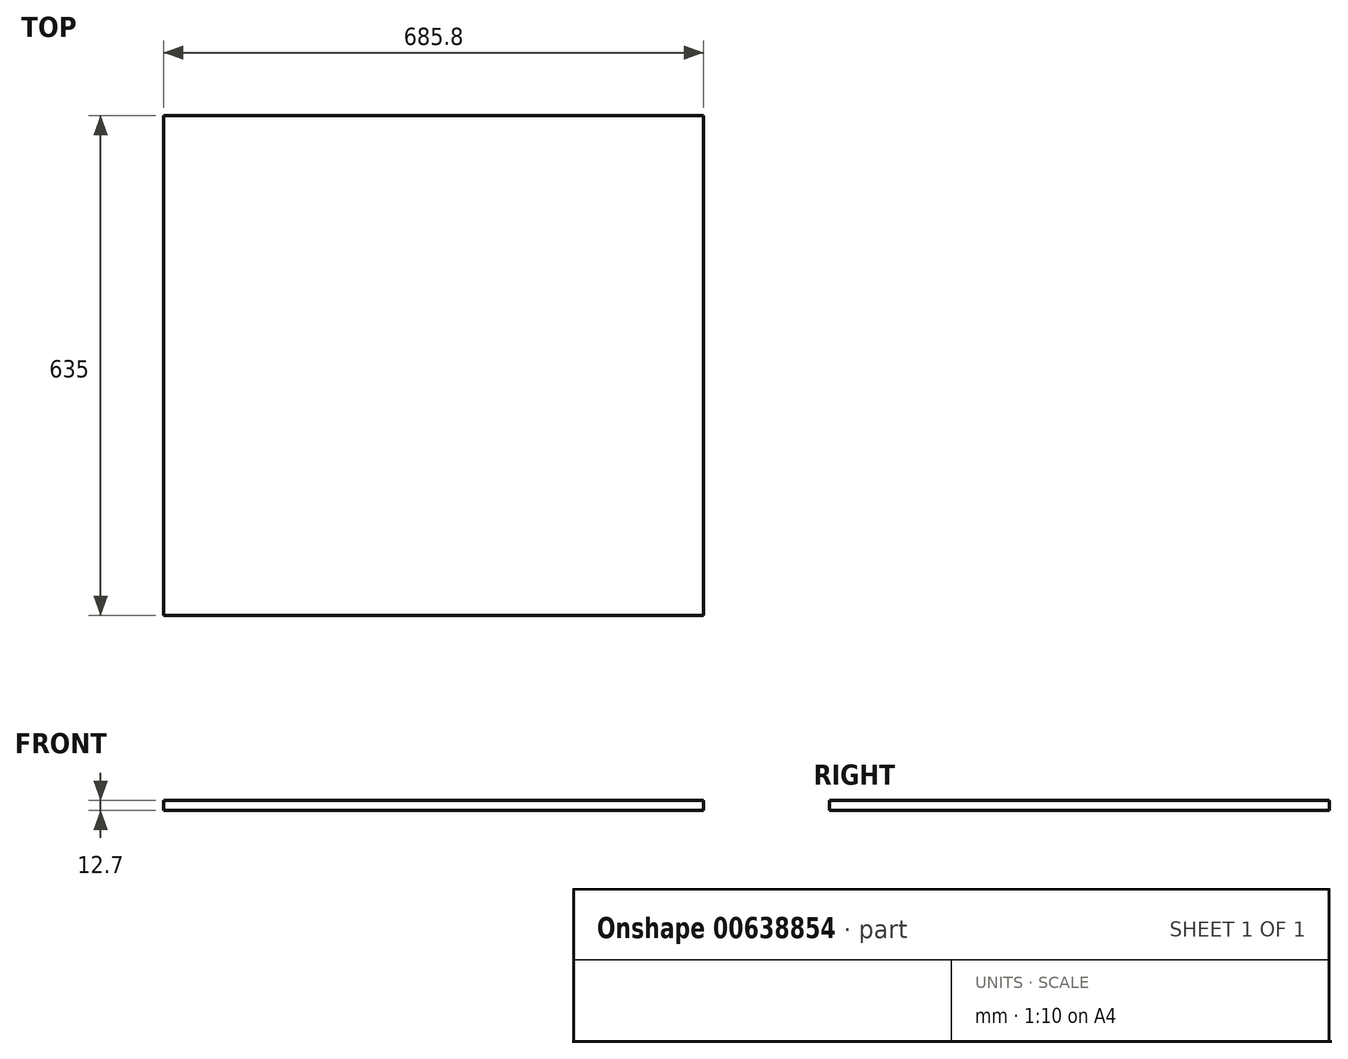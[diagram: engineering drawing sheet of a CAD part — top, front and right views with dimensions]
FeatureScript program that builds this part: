
annotation { "Feature Type Name" : "Feature", "Feature Type Description" : "" }
export const myFeature = defineFeature(function(context is Context, id is Id, definition is map)
    precondition{}
    {
        {
            var Q0;
            Q0=qCreatedBy(makeId("Top.planeOp"),FACE);
            var sketch = newSketch(context, id + "F0", { "sketchPlane" : qUnion([Q0])});
            skLineSegment(sketch, "E0.bottom", {"start": v(342.9, 317.5) * mm, "end": v(-342.9, 317.5) * mm});
            skLineSegment(sketch, "E0.top", {"start": v(342.9, -317.5) * mm, "end": v(-342.9, -317.5) * mm});
            skLineSegment(sketch, "E0.left", {"start": v(342.9, 317.5) * mm, "end": v(342.9, -317.5) * mm});
            skLineSegment(sketch, "E0.right", {"start": v(-342.9, 317.5) * mm, "end": v(-342.9, -317.5) * mm});
            skPoint(sketch, "E0.middle", {"position": v(0, 0) * mm});
            skSolve(sketch);
        }
        {
            var Q0;
            Q0=makeQuery(id+"F0.imprint","IMPRINT",FACE,{"disambiguationData":[TD([[makeQuery(id+"F0.imprint","IMPRINT",EDGE,{"derivedFrom":sQuery(id+"F0.wireOp",EDGE,"E0.bottom")}),1.0]])]});
            extrude(context, id + "F1", {"entities" : qUnion([Q0]), "depth" : 12.7 * mm, "offsetDistance" : 25.4 * mm});
        }
    });
